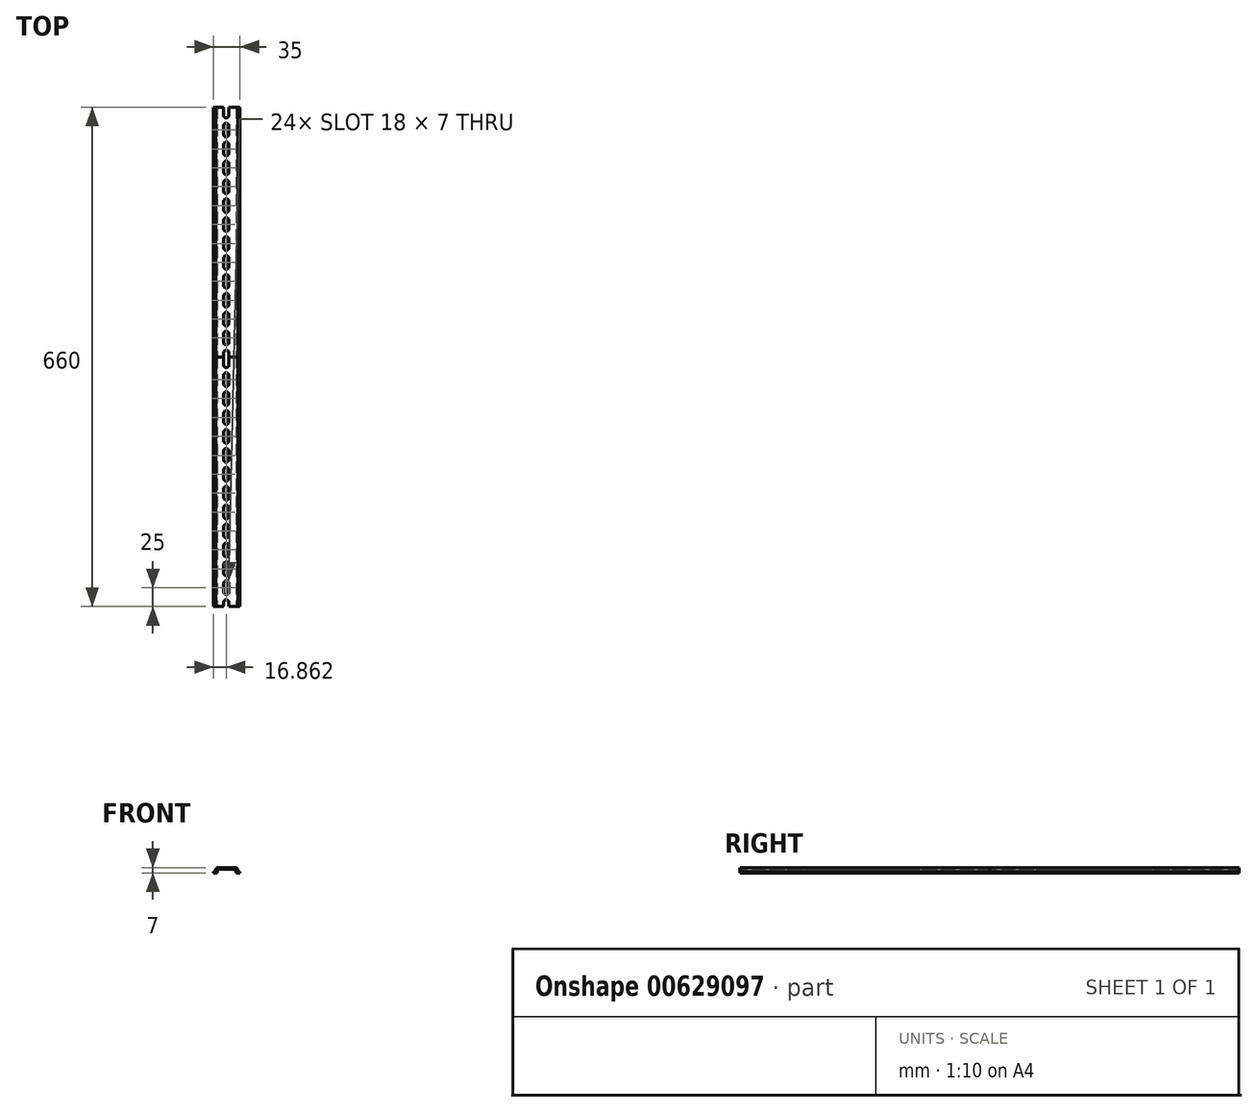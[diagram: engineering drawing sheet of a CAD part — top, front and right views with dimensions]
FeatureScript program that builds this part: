
annotation { "Feature Type Name" : "Feature", "Feature Type Description" : "" }
export const myFeature = defineFeature(function(context is Context, id is Id, definition is map)
    precondition{}
    {
        {
            var Q0;
            Q0=qCreatedBy(makeId("Front.planeOp"),FACE);
            var sketch = newSketch(context, id + "F0", { "sketchPlane" : qUnion([Q0])});
            skLineSegment(sketch, "E0", {"start": v(-16.86, 0) * mm, "end": v(-12.86, 0) * mm});
            skLineSegment(sketch, "E1", {"start": v(-11.86, 1) * mm, "end": v(-11.86, 4) * mm});
            skLineSegment(sketch, "E2", {"start": v(-10.86, 5) * mm, "end": v(12.14, 5) * mm});
            skLineSegment(sketch, "E3", {"start": v(13.14, 4) * mm, "end": v(13.14, 1) * mm});
            skLineSegment(sketch, "E4", {"start": v(14.14, 0) * mm, "end": v(18.14, 0) * mm});
            skPoint(sketch, "E5.visualSharp", {"position": v(-11.86, 0) * mm});
            skArc(sketch, "E5.filletArc", {"start": v(-12.86, 0) * mm, "mid": v(-12.15, 0.3) * mm, "end": v(-11.86, 1) * mm});
            skPoint(sketch, "E6.visualSharp", {"position": v(-11.86, 5) * mm});
            skArc(sketch, "E6.filletArc", {"start": v(-10.86, 5) * mm, "mid": v(-11.57, 4.7) * mm, "end": v(-11.86, 4) * mm});
            skPoint(sketch, "E7.visualSharp", {"position": v(13.14, 5) * mm});
            skArc(sketch, "E7.filletArc", {"start": v(13.14, 4) * mm, "mid": v(12.85, 4.7) * mm, "end": v(12.14, 5) * mm});
            skPoint(sketch, "E8.visualSharp", {"position": v(13.14, 0) * mm});
            skArc(sketch, "E8.filletArc", {"start": v(13.14, 1) * mm, "mid": v(13.43, 0.3) * mm, "end": v(14.14, 0) * mm});
            skLineSegment(sketch, "E9.0", {"start": v(15.14, 2) * mm, "end": v(18.14, 2) * mm});
            skLineSegment(sketch, "E9.1", {"start": v(15.14, 4) * mm, "end": v(15.14, 2) * mm});
            skArc(sketch, "E9.2", {"start": v(15.14, 4) * mm, "mid": v(14.26, 6.12) * mm, "end": v(12.14, 7) * mm});
            skLineSegment(sketch, "E9.3", {"start": v(-16.86, 2) * mm, "end": v(-13.86, 2) * mm});
            skLineSegment(sketch, "E9.4", {"start": v(-13.86, 2) * mm, "end": v(-13.86, 4) * mm});
            skArc(sketch, "E9.5", {"start": v(-10.86, 7) * mm, "mid": v(-12.98, 6.12) * mm, "end": v(-13.86, 4) * mm});
            skLineSegment(sketch, "E9.6", {"start": v(-10.86, 7) * mm, "end": v(12.14, 7) * mm});
            skLineSegment(sketch, "E10", {"start": v(-16.86, 0) * mm, "end": v(-16.86, 2) * mm});
            skLineSegment(sketch, "E11", {"start": v(18.14, 0) * mm, "end": v(18.14, 2) * mm});
            skSolve(sketch);
        }
        {
            var Q0;
            Q0=qSketchRegion(id+"F0",true);
            extrude(context, id + "F1", {"entities" : qUnion([Q0]), "oppositeDirection" : true, "depth" : 330 * mm, "offsetDistance" : 25 * mm});
        }
        {
            var Q0;
            Q0=makeQuery(id+"F1.opExtrude","SWEPT_FACE",FACE,{"disambiguationData":[OSD([sQuery(id+"F0.wireOp",EDGE,"E9.6")])]});
            var sketch = newSketch(context, id + "F2", { "sketchPlane" : qUnion([Q0])});
            skCircle(sketch, "E12", {"center": v(0, 5.5) * mm, "radius": 3.5 * mm});
            skCircle(sketch, "E13", {"center": v(0, -5.5) * mm, "radius": 3.5 * mm});
            skPoint(sketch, "E14", {"position": v(0, 9) * mm});
            skPoint(sketch, "E15", {"position": v(0, -9) * mm});
            skLineSegment(sketch, "E16", {"start": v(-3.5, 5.65) * mm, "end": v(-3.5, -5.65) * mm});
            skLineSegment(sketch, "E17", {"start": v(3.5, 5.52) * mm, "end": v(3.5, -5.52) * mm});
            skCircle(sketch, "E18.0.1.0", {"center": v(0, 30.5) * mm, "radius": 3.5 * mm});
            skLineSegment(sketch, "E18.0.1.1", {"start": v(-3.5, 30.65) * mm, "end": v(-3.5, 19.35) * mm});
            skLineSegment(sketch, "E18.0.1.2", {"start": v(3.5, 30.52) * mm, "end": v(3.5, 19.48) * mm});
            skCircle(sketch, "E18.0.1.3", {"center": v(0, 19.5) * mm, "radius": 3.5 * mm});
            skCircle(sketch, "E18.0.2.0", {"center": v(0, 55.5) * mm, "radius": 3.5 * mm});
            skLineSegment(sketch, "E18.0.2.1", {"start": v(-3.5, 55.65) * mm, "end": v(-3.5, 44.35) * mm});
            skLineSegment(sketch, "E18.0.2.2", {"start": v(3.5, 55.52) * mm, "end": v(3.5, 44.48) * mm});
            skCircle(sketch, "E18.0.2.3", {"center": v(0, 44.5) * mm, "radius": 3.5 * mm});
            skCircle(sketch, "E18.0.3.0", {"center": v(0, 80.5) * mm, "radius": 3.5 * mm});
            skLineSegment(sketch, "E18.0.3.1", {"start": v(-3.5, 80.65) * mm, "end": v(-3.5, 69.35) * mm});
            skLineSegment(sketch, "E18.0.3.2", {"start": v(3.5, 80.52) * mm, "end": v(3.5, 69.48) * mm});
            skCircle(sketch, "E18.0.3.3", {"center": v(0, 69.5) * mm, "radius": 3.5 * mm});
            skCircle(sketch, "E18.0.4.0", {"center": v(0, 105.5) * mm, "radius": 3.5 * mm});
            skLineSegment(sketch, "E18.0.4.1", {"start": v(-3.5, 105.65) * mm, "end": v(-3.5, 94.35) * mm});
            skLineSegment(sketch, "E18.0.4.2", {"start": v(3.5, 105.52) * mm, "end": v(3.5, 94.48) * mm});
            skCircle(sketch, "E18.0.4.3", {"center": v(0, 94.5) * mm, "radius": 3.5 * mm});
            skCircle(sketch, "E18.0.5.0", {"center": v(0, 130.5) * mm, "radius": 3.5 * mm});
            skLineSegment(sketch, "E18.0.5.1", {"start": v(-3.5, 130.65) * mm, "end": v(-3.5, 119.35) * mm});
            skLineSegment(sketch, "E18.0.5.2", {"start": v(3.5, 130.52) * mm, "end": v(3.5, 119.48) * mm});
            skCircle(sketch, "E18.0.5.3", {"center": v(0, 119.5) * mm, "radius": 3.5 * mm});
            skCircle(sketch, "E18.0.6.0", {"center": v(0, 155.5) * mm, "radius": 3.5 * mm});
            skLineSegment(sketch, "E18.0.6.1", {"start": v(-3.5, 155.65) * mm, "end": v(-3.5, 144.35) * mm});
            skLineSegment(sketch, "E18.0.6.2", {"start": v(3.5, 155.52) * mm, "end": v(3.5, 144.48) * mm});
            skCircle(sketch, "E18.0.6.3", {"center": v(0, 144.5) * mm, "radius": 3.5 * mm});
            skCircle(sketch, "E18.0.7.0", {"center": v(0, 180.5) * mm, "radius": 3.5 * mm});
            skLineSegment(sketch, "E18.0.7.1", {"start": v(-3.5, 180.65) * mm, "end": v(-3.5, 169.35) * mm});
            skLineSegment(sketch, "E18.0.7.2", {"start": v(3.5, 180.52) * mm, "end": v(3.5, 169.48) * mm});
            skCircle(sketch, "E18.0.7.3", {"center": v(0, 169.5) * mm, "radius": 3.5 * mm});
            skCircle(sketch, "E18.0.8.0", {"center": v(0, 205.5) * mm, "radius": 3.5 * mm});
            skLineSegment(sketch, "E18.0.8.1", {"start": v(-3.5, 205.65) * mm, "end": v(-3.5, 194.35) * mm});
            skLineSegment(sketch, "E18.0.8.2", {"start": v(3.5, 205.52) * mm, "end": v(3.5, 194.48) * mm});
            skCircle(sketch, "E18.0.8.3", {"center": v(0, 194.5) * mm, "radius": 3.5 * mm});
            skCircle(sketch, "E18.0.9.0", {"center": v(0, 230.5) * mm, "radius": 3.5 * mm});
            skLineSegment(sketch, "E18.0.9.1", {"start": v(-3.5, 230.65) * mm, "end": v(-3.5, 219.35) * mm});
            skLineSegment(sketch, "E18.0.9.2", {"start": v(3.5, 230.52) * mm, "end": v(3.5, 219.48) * mm});
            skCircle(sketch, "E18.0.9.3", {"center": v(0, 219.5) * mm, "radius": 3.5 * mm});
            skCircle(sketch, "E18.0.10.0", {"center": v(0, 255.5) * mm, "radius": 3.5 * mm});
            skLineSegment(sketch, "E18.0.10.1", {"start": v(-3.5, 255.65) * mm, "end": v(-3.5, 244.35) * mm});
            skLineSegment(sketch, "E18.0.10.2", {"start": v(3.5, 255.52) * mm, "end": v(3.5, 244.48) * mm});
            skCircle(sketch, "E18.0.10.3", {"center": v(0, 244.5) * mm, "radius": 3.5 * mm});
            skCircle(sketch, "E18.0.11.0", {"center": v(0, 280.5) * mm, "radius": 3.5 * mm});
            skLineSegment(sketch, "E18.0.11.1", {"start": v(-3.5, 280.65) * mm, "end": v(-3.5, 269.35) * mm});
            skLineSegment(sketch, "E18.0.11.2", {"start": v(3.5, 280.52) * mm, "end": v(3.5, 269.48) * mm});
            skCircle(sketch, "E18.0.11.3", {"center": v(0, 269.5) * mm, "radius": 3.5 * mm});
            skCircle(sketch, "E18.0.12.0", {"center": v(0, 305.5) * mm, "radius": 3.5 * mm});
            skLineSegment(sketch, "E18.0.12.1", {"start": v(-3.5, 305.65) * mm, "end": v(-3.5, 294.35) * mm});
            skLineSegment(sketch, "E18.0.12.2", {"start": v(3.5, 305.52) * mm, "end": v(3.5, 294.48) * mm});
            skCircle(sketch, "E18.0.12.3", {"center": v(0, 294.5) * mm, "radius": 3.5 * mm});
            skLineSegment(sketch, "E18.direction1", {"start": v(0, 5.5) * mm, "end": v(44.8, 5.5) * mm, "construction": true});
            skLineSegment(sketch, "E18.direction2", {"start": v(0, 5.5) * mm, "end": v(0, 30.5) * mm, "construction": true});
            skCircle(sketch, "E19.0.0.13", {"center": v(0, 330.5) * mm, "radius": 3.5 * mm});
            skLineSegment(sketch, "E19.2.0.13", {"start": v(-3.5, 330.65) * mm, "end": v(-3.5, 319.35) * mm});
            skLineSegment(sketch, "E19.5.0.13", {"start": v(3.5, 330.52) * mm, "end": v(3.5, 319.48) * mm});
            skCircle(sketch, "E19.8.0.13", {"center": v(0, 319.5) * mm, "radius": 3.5 * mm});
            skSolve(sketch);
        }
        {
            var Q0;
            Q0=qSketchRegion(id+"F2",true);
            extrude(context, id + "F3", {"entities" : qUnion([Q0]), "operationType" : NewBodyOperationType.REMOVE, "oppositeDirection" : true, "depth" : 25 * mm, "offsetDistance" : 25 * mm});
        }
        {
            var Q0;
            Q0=makeQuery(id+"F1.opExtrude","SWEPT_BODY",BODY,{"disambiguationData":[OSD([sQuery(id+"F0.wireOp",EDGE,"E0"),sQuery(id+"F0.wireOp",EDGE,"E1"),sQuery(id+"F0.wireOp",EDGE,"E2"),sQuery(id+"F0.wireOp",EDGE,"E3"),sQuery(id+"F0.wireOp",EDGE,"E4"),sQuery(id+"F0.wireOp",EDGE,"E5.filletArc"),sQuery(id+"F0.wireOp",EDGE,"E6.filletArc"),sQuery(id+"F0.wireOp",EDGE,"E7.filletArc"),sQuery(id+"F0.wireOp",EDGE,"E8.filletArc"),sQuery(id+"F0.wireOp",EDGE,"E9.0"),sQuery(id+"F0.wireOp",EDGE,"E9.1"),sQuery(id+"F0.wireOp",EDGE,"E9.2"),sQuery(id+"F0.wireOp",EDGE,"E9.3"),sQuery(id+"F0.wireOp",EDGE,"E9.4"),sQuery(id+"F0.wireOp",EDGE,"E9.5"),sQuery(id+"F0.wireOp",EDGE,"E9.6"),sQuery(id+"F0.wireOp",EDGE,"E10"),sQuery(id+"F0.wireOp",EDGE,"E11")])]});
            var Q1;
            Q1=makeQuery(id+"F1.opExtrude","SWEPT_EDGE",EDGE,{"disambiguationData":[OSD([sQuery(id+"F0.wireOp",EDGE,"E9.0"),sQuery(id+"F0.wireOp",EDGE,"E11")])]});
            transform(context, id + "F4", {"entities" : qUnion([Q0]), "transformType" : TransformType.TRANSLATION_ENTITY, "oppositeDirectionEntity" : false, "transformLine" : qUnion([Q1]), "makeCopy" : true});
        }
    });
